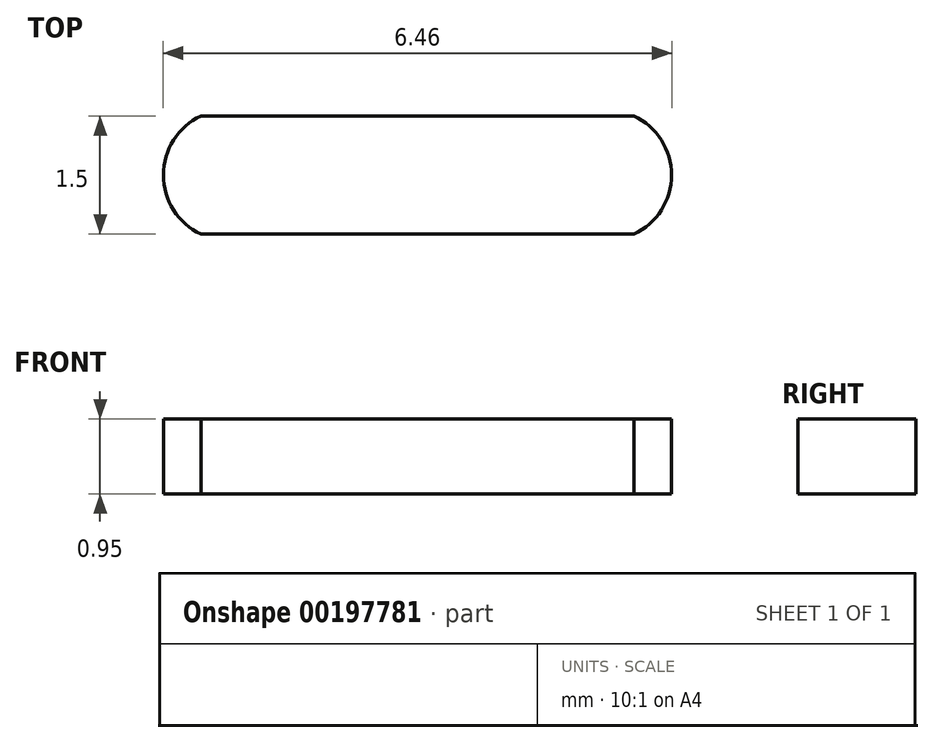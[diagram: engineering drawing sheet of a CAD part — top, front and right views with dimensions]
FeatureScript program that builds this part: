
annotation { "Feature Type Name" : "Feature", "Feature Type Description" : "" }
export const myFeature = defineFeature(function(context is Context, id is Id, definition is map)
    precondition{}
    {
        {
            var Q0;
            Q0=qCreatedBy(makeId("Top.planeOp"),FACE);
            var sketch = newSketch(context, id + "F0", { "sketchPlane" : qUnion([Q0])});
            skLineSegment(sketch, "E0.bottom", {"start": v(2.75, -0.75) * mm, "end": v(-2.75, -0.75) * mm});
            skLineSegment(sketch, "E0.top", {"start": v(2.75, 0.75) * mm, "end": v(-2.75, 0.75) * mm});
            skLineSegment(sketch, "E0.left", {"start": v(2.75, -0.75) * mm, "end": v(2.75, 0.75) * mm});
            skLineSegment(sketch, "E0.right", {"start": v(-2.75, -0.75) * mm, "end": v(-2.75, 0.75) * mm});
            skPoint(sketch, "E0.middle", {"position": v(0, 0) * mm});
            skArc(sketch, "E1", {"start": v(-2.75, 0.75) * mm, "mid": v(-3.23, 0) * mm, "end": v(-2.75, -0.75) * mm});
            skArc(sketch, "E2", {"start": v(2.75, -0.75) * mm, "mid": v(3.23, 0) * mm, "end": v(2.75, 0.75) * mm});
            skSolve(sketch);
        }
        {
            var Q0;
            Q0 = qSketchRegion(id + "F0", true);
            extrude(context, id + "F1", {"entities" : qUnion([Q0]), "depth" : 0.95 * mm});
        }
    });
